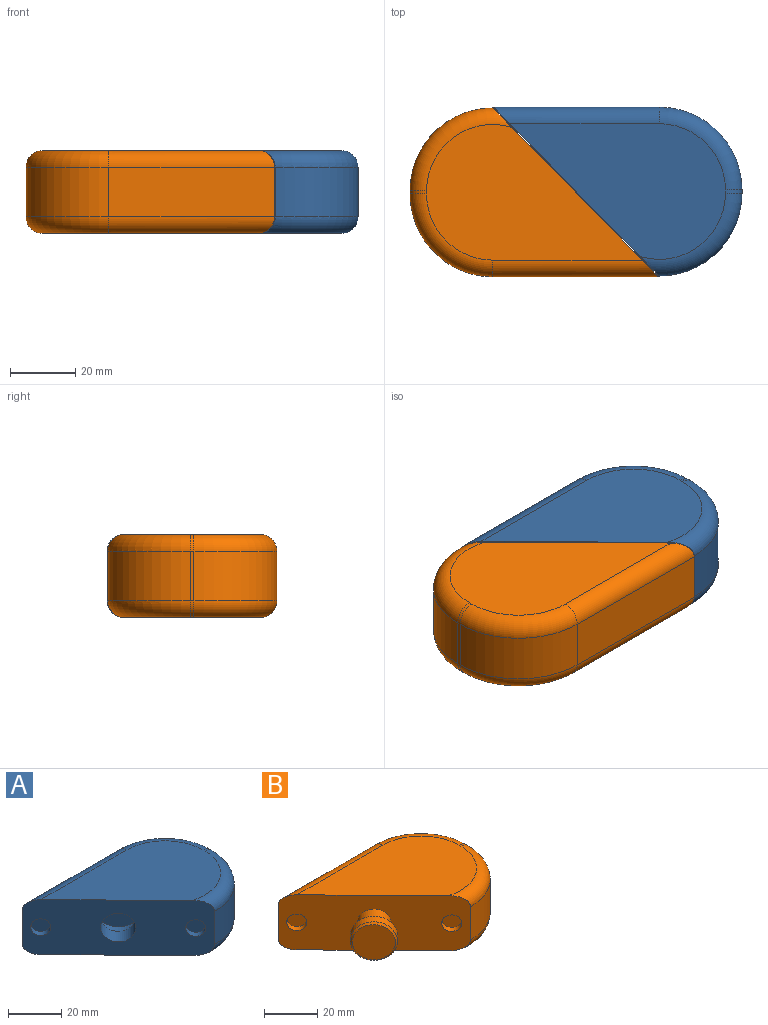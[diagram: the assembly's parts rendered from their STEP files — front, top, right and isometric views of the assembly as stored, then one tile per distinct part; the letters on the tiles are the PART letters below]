
ASSEMBLY  parts=2 mates=1
PART A: 23 faces, bbox 78.3x56x25.4 mm
  f0: plane 50.8x15.24mm, normal (0,1,0), area 774.2mm2, adj f1,f4,f7,f11
  f1: plane 51.77x50.8mm, normal (-0.71,-0.7,0), area 1582.2mm2, adj f0,f2,f5,f6,f7,f10,f11,f14
  f2: cylinder r=25.4mm len=25.4mm, axis (0,0,-1), area 608mm2, adj f1,f3,f10,f14
  f3: plane 15.24x0.97mm, normal (1,0,0), area 14.8mm2, adj f2,f4,f9,f13
  f4: cylinder r=25.4mm len=25.4mm, axis (0,0,-1), area 608mm2, adj f0,f3,f8,f12
  f5: plane 66.14x41.61mm, normal (0,0,1), area 1724mm2, adj f1,f11,f12,f13,f14
  f6: plane 66.14x41.61mm, normal (0,0,-1), area 1724mm2, adj f1,f7,f8,f9,f10
  f7: cylinder r=5.08mm len=50.8mm, axis (-1,0,0), area 390.9mm2, adj f0,f1,f6,f8
  f8: torus R=20.32mm, axis (0,0,1), area 295.2mm2, adj f4,f6,f7,f9
  f9: cylinder r=5.08mm len=5.08mm, axis (0,1,0), area 7.7mm2, adj f3,f6,f8,f10
  f10: torus R=20.32mm, axis (0,0,1), area 311mm2, adj f1,f2,f6,f9
  f11: cylinder r=5.08mm len=50.8mm, axis (1,0,0), area 390.9mm2, adj f0,f1,f5,f12
  f12: torus R=20.32mm, axis (0,0,1), area 295.2mm2, adj f4,f5,f11,f13
  f13: cylinder r=5.08mm len=5.08mm, axis (0,-1,0), area 7.7mm2, adj f3,f5,f12,f14
  f14: torus R=20.32mm, axis (0,0,1), area 311mm2, adj f1,f2,f5,f13
  f15: cylinder r=3.81mm len=7.62mm, axis (-0.71,-0.7,0), area 60.8mm2, adj f1,f16
  f16: plane 7.62x5.44mm, normal (-0.71,-0.7,0), area 45.6mm2, adj f15
  f17: cylinder r=3.81mm len=7.62mm, axis (-0.71,-0.7,0), area 60.8mm2, adj f1,f18
  f18: plane 7.62x5.44mm, normal (-0.71,-0.7,0), area 45.6mm2, adj f17
  f19: cylinder r=6.6mm len=14.23mm, axis (-0.71,-0.7,0), area 284.6mm2, adj f1,f20
  f20: plane 17.78x12.69mm, normal (0.71,0.7,0), area 111.3mm2, adj f19,f21
  f21: cylinder r=8.89mm len=17.78mm, axis (0.71,0.7,0), area 340.5mm2, adj f20,f22
  f22: plane 17.78x12.69mm, normal (-0.71,-0.7,0), area 248.3mm2, adj f21
PART B: 25 faces, bbox 78.3x56x25.4 mm
  f0: cylinder r=6.35mm len=14.4mm, axis (0.71,0.7,0), area 304mm2, adj f2,f17
  f1: plane 50.8x15.24mm, normal (0,1,0), area 774.2mm2, adj f2,f5,f8,f12
  f2: plane 51.77x50.8mm, normal (-0.71,-0.7,0), area 1592.5mm2, adj f0,f1,f3,f6,f7,f8,f11,f12
  f3: cylinder r=25.4mm len=25.4mm, axis (0,0,-1), area 608mm2, adj f2,f4,f11,f15
  f4: plane 15.24x0.97mm, normal (1,0,0), area 14.8mm2, adj f3,f5,f10,f14
  f5: cylinder r=25.4mm len=25.4mm, axis (0,0,-1), area 608mm2, adj f1,f4,f9,f13
  f6: plane 66.14x41.61mm, normal (0,0,1), area 1724mm2, adj f2,f12,f13,f14,f15
  f7: plane 66.14x41.61mm, normal (0,0,-1), area 1724mm2, adj f2,f8,f9,f10,f11
  f8: cylinder r=5.08mm len=50.8mm, axis (-1,0,0), area 390.9mm2, adj f1,f2,f7,f9
  f9: torus R=20.32mm, axis (0,0,1), area 295.2mm2, adj f5,f7,f8,f10
  f10: cylinder r=5.08mm len=5.08mm, axis (0,1,0), area 7.7mm2, adj f4,f7,f9,f11
  f11: torus R=20.32mm, axis (0,0,1), area 311mm2, adj f2,f3,f7,f10
  f12: cylinder r=5.08mm len=50.8mm, axis (1,0,0), area 390.9mm2, adj f1,f2,f6,f13
  f13: torus R=20.32mm, axis (0,0,1), area 295.2mm2, adj f5,f6,f12,f14
  f14: cylinder r=5.08mm len=5.08mm, axis (0,-1,0), area 7.7mm2, adj f4,f6,f13,f15
  f15: torus R=20.32mm, axis (0,0,1), area 311mm2, adj f2,f3,f6,f14
  f16: cylinder r=8.89mm len=17.78mm, axis (-0.71,-0.7,0), area 198.6mm2, adj f23,f24
  f17: plane 16.26x11.6mm, normal (0.71,0.7,0), area 80.9mm2, adj f0,f23
  f18: plane 16.26x11.6mm, normal (-0.71,-0.7,0), area 207.5mm2, adj f24
  f19: cylinder r=3.81mm len=7.62mm, axis (-0.71,-0.7,0), area 60.8mm2, adj f2,f20
  f20: plane 7.62x5.44mm, normal (-0.71,-0.7,0), area 45.6mm2, adj f19
  f21: cylinder r=3.81mm len=7.62mm, axis (-0.71,-0.7,0), area 60.8mm2, adj f2,f22
  f22: plane 7.62x5.44mm, normal (-0.71,-0.7,0), area 45.6mm2, adj f21
  f23: cone r=8.89mm half-angle=45deg, axis (-0.71,-0.7,0), area 57.6mm2, adj f16,f17
  f24: cone r=8.13mm half-angle=45deg, axis (0.71,0.7,0), area 57.6mm2, adj f16,f18
PLACE A t=(2.56,1.78,10.31)mm
PLACE B rot(axis=(0,0,1),180deg) t=(-32.72,26.65,10.31)mm
MATE revolute B.f23 <-> A.f21  axis (0.71,0.7,0) through (-6.13,22.99,23.01)mm
